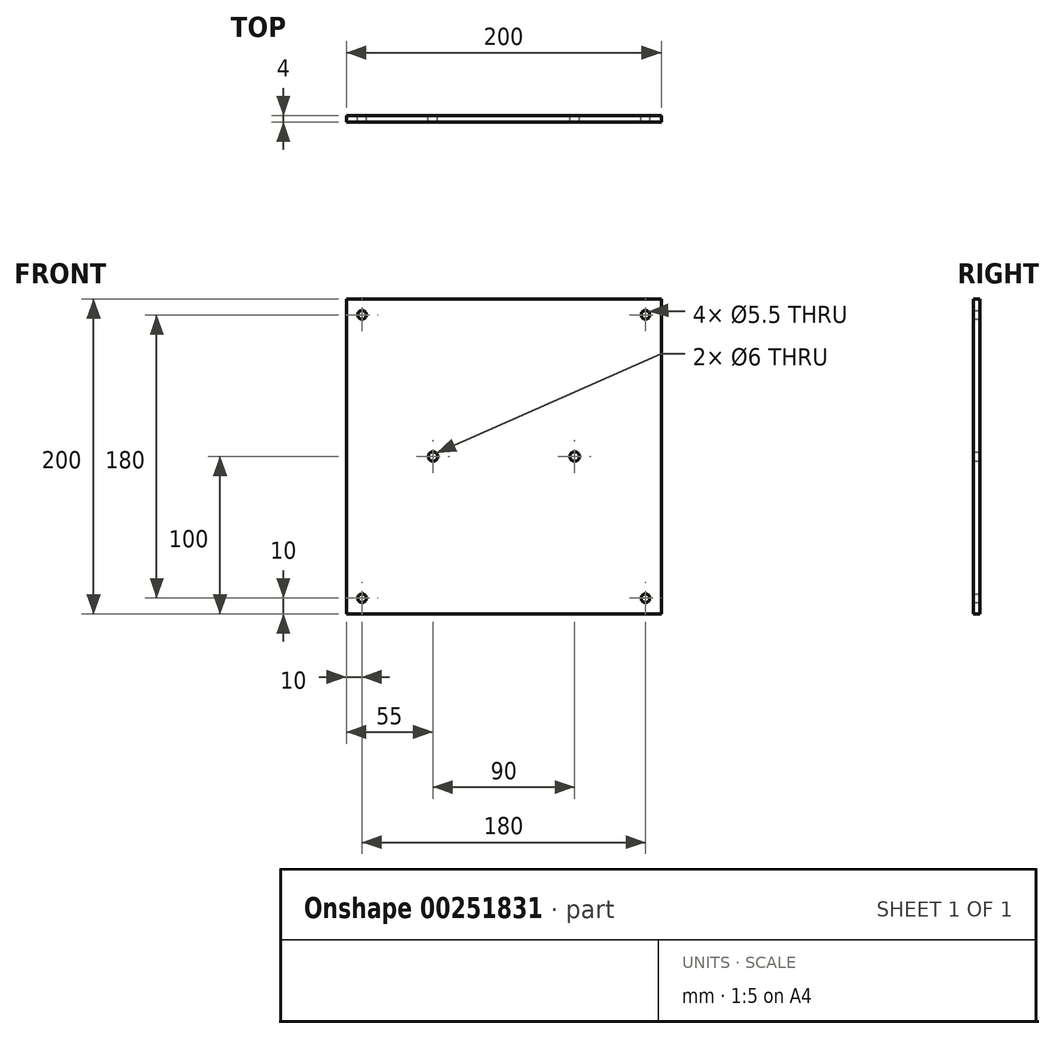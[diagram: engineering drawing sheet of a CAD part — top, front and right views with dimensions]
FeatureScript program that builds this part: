
annotation { "Feature Type Name" : "Feature", "Feature Type Description" : "" }
export const myFeature = defineFeature(function(context is Context, id is Id, definition is map)
    precondition{}
    {
        {
            var Q0;
            Q0=qCreatedBy(makeId("Front.planeOp"),FACE);
            var sketch = newSketch(context, id + "F0", { "sketchPlane" : qUnion([Q0])});
            skLineSegment(sketch, "E0.bottom", {"start": v(100, -100) * mm, "end": v(-100, -100) * mm});
            skLineSegment(sketch, "E0.top", {"start": v(100, 100) * mm, "end": v(-100, 100) * mm});
            skLineSegment(sketch, "E0.left", {"start": v(100, -100) * mm, "end": v(100, 100) * mm});
            skLineSegment(sketch, "E0.right", {"start": v(-100, -100) * mm, "end": v(-100, 100) * mm});
            skPoint(sketch, "E0.middle", {"position": v(0, 0) * mm});
            skCircle(sketch, "E1", {"center": v(-90, 90) * mm, "radius": 2.75 * mm});
            skCircle(sketch, "E2", {"center": v(90, 90) * mm, "radius": 2.75 * mm});
            skCircle(sketch, "E3", {"center": v(-90, -90) * mm, "radius": 2.75 * mm});
            skCircle(sketch, "E4", {"center": v(90, -90) * mm, "radius": 2.75 * mm});
            skLineSegment(sketch, "E5", {"start": v(-64.55, 0) * mm, "end": v(59.8, 0) * mm, "construction": true});
            skCircle(sketch, "E6", {"center": v(-45, 0) * mm, "radius": 3 * mm});
            skCircle(sketch, "E7", {"center": v(45, 0) * mm, "radius": 3 * mm});
            skSolve(sketch);
        }
        {
            var Q0;
            Q0=makeQuery(id+"F0.imprint","IMPRINT",FACE,{"disambiguationData":[TD([[makeQuery(id+"F0.imprint","IMPRINT",EDGE,{"derivedFrom":sQuery(id+"F0.wireOp",EDGE,"E0.bottom")}),-1.0]])]});
            extrude(context, id + "F1", {"entities" : qUnion([Q0]), "depth" : 4 * mm});
        }
    });
